# Revit family: 1220039 - Maris MRX110-70
name_source: partatom
category: Plumbing Fixtures
revit_build: Autodesk Revit 2018 (Build: 20170927_1515(x64)
units: mm (PartAtom-declared; Revit-internal decimal feet)

## family parameters
Always vertical = Yes
Cut with Voids When Loaded = No
OmniClass Number = 23.45.05.14.99
OmniClass Title = Other Sanitary Washing Plumbing Fixtures
Part Type = Normal
Room Calculation Point = No
Round Connector Dimension = Use Diameter
Shared = No
Work Plane-Based = No

## types (1)
- Maris MRX110-70
    Bowl Dimensions = 700mm x 400mm x 180mm
    CW Connection = Yes
    CWFU = 0
    Default Elevation = 900.0
    HW Connection = Yes
    HWFU = 0
    Manufacturer = Franke South Africa (Pty) Ltd
    Material = Austenitic Stainless Steel
    Model = Maris MRX110-70
    Product Code = 1220039
    Sink Dimensions = 740mm x 440mm
    Vent Connection = No
    WFU = 0
    Waste Connection = Yes

## geometry (parser evidence)
native form markers: Blend x8, Sweep x2
no freeform markers — native parametric forms only
